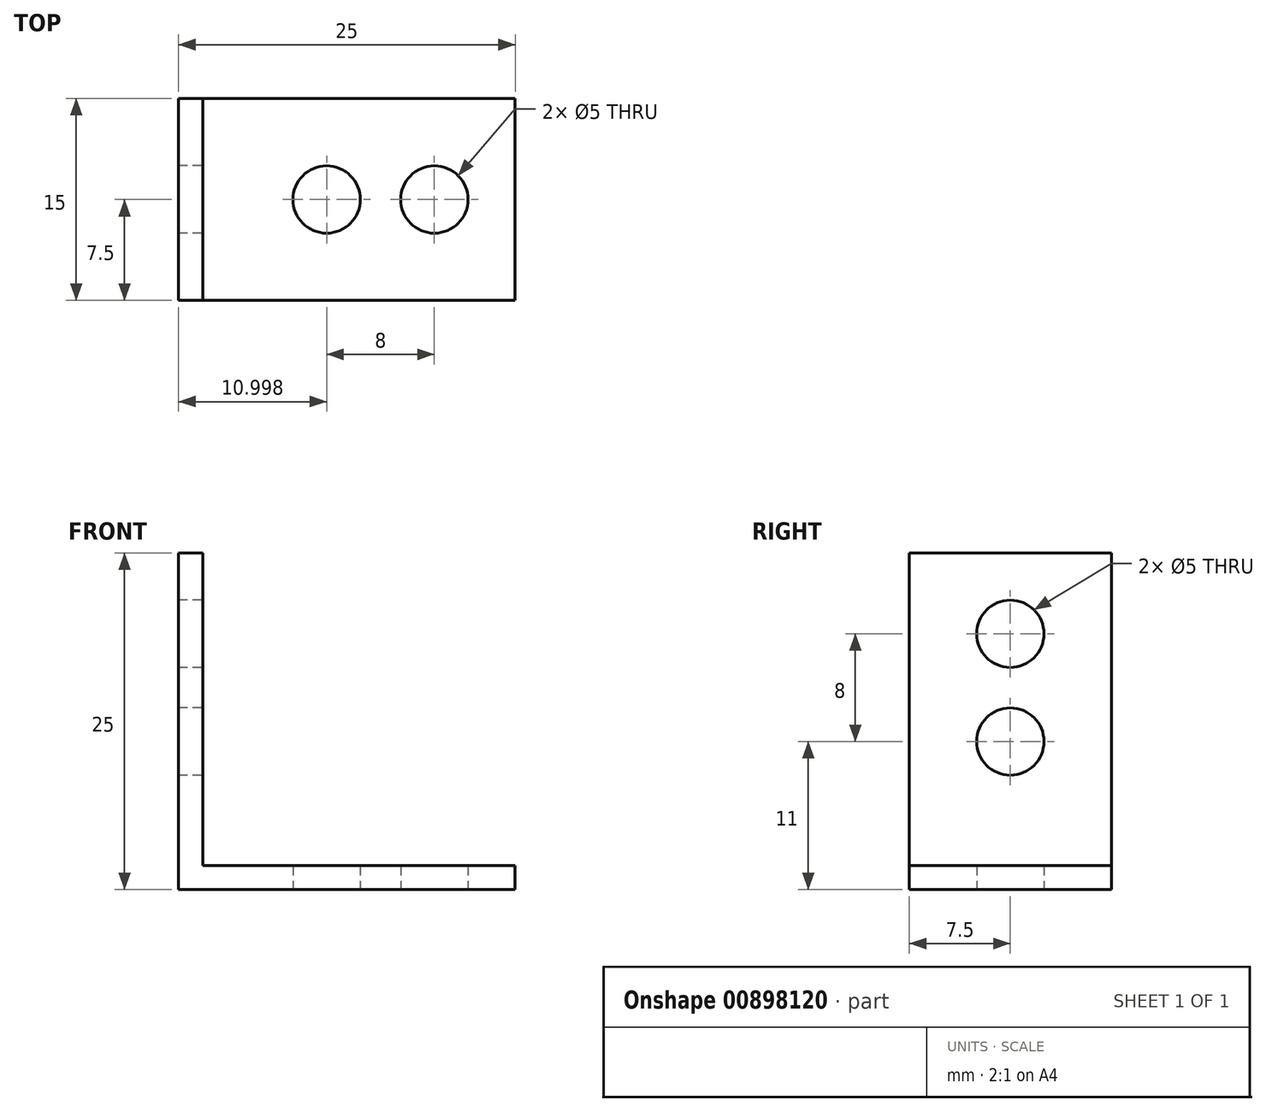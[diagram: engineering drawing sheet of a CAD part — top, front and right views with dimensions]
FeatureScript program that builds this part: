
annotation { "Feature Type Name" : "Feature", "Feature Type Description" : "" }
export const myFeature = defineFeature(function(context is Context, id is Id, definition is map)
    precondition{}
    {
        {
            var Q0;
            Q0=qCreatedBy(makeId("Front.planeOp"),FACE);
            var sketch = newSketch(context, id + "F0", { "sketchPlane" : qUnion([Q0])});
            skLineSegment(sketch, "E0.bottom", {"start": v(-6.03, 0) * mm, "end": v(18.97, 0) * mm});
            skLineSegment(sketch, "E0.top", {"start": v(-6.03, 1.8) * mm, "end": v(18.97, 1.8) * mm});
            skLineSegment(sketch, "E0.left", {"start": v(-6.03, 0) * mm, "end": v(-6.03, 1.8) * mm});
            skLineSegment(sketch, "E0.right", {"start": v(18.97, 0) * mm, "end": v(18.97, 1.8) * mm});
            skLineSegment(sketch, "E1.bottom", {"start": v(-6.03, 0) * mm, "end": v(-4.23, 0) * mm});
            skLineSegment(sketch, "E1.top", {"start": v(-6.03, 25) * mm, "end": v(-4.23, 25) * mm});
            skLineSegment(sketch, "E1.left", {"start": v(-6.03, 0) * mm, "end": v(-6.03, 25) * mm});
            skLineSegment(sketch, "E1.right", {"start": v(-4.23, 0) * mm, "end": v(-4.23, 25) * mm});
            skSolve(sketch);
        }
        {
            var Q0;
            Q0 = qSketchRegion(id + "F0", true);
            extrude(context, id + "F1", {"entities" : qUnion([Q0]), "depth" : 15 * mm, "offsetDistance" : 25 * mm});
        }
        {
            var Q0;
            Q0=makeQuery(id+"F1.opExtrude","SWEPT_FACE",FACE,{"disambiguationData":[OSD([sQuery(id+"F0.wireOp",EDGE,"E1.left")])]});
            var sketch = newSketch(context, id + "F2", { "sketchPlane" : qUnion([Q0])});
            skPoint(sketch, "E2", {"position": v(0, 25) * mm});
            skPoint(sketch, "E3", {"position": v(15, 25) * mm});
            skPoint(sketch, "E4", {"position": v(15, 0) * mm});
            skPoint(sketch, "E5", {"position": v(0, 0) * mm});
            skPoint(sketch, "E6", {"position": v(7.5, 25) * mm});
            skPoint(sketch, "E7", {"position": v(7.5, 0) * mm});
            skPoint(sketch, "E8", {"position": v(7.5, 11) * mm});
            skPoint(sketch, "E9", {"position": v(7.5, 19) * mm});
            skCircle(sketch, "E10", {"center": v(7.5, 19) * mm, "radius": 2.5 * mm});
            skCircle(sketch, "E11", {"center": v(7.5, 11) * mm, "radius": 2.5 * mm});
            skSolve(sketch);
        }
        {
            var Q0;
            Q0=makeQuery(id+"F1.opExtrude","SWEPT_FACE",FACE,{"disambiguationData":[OSD([sQuery(id+"F0.wireOp",EDGE,"E0.bottom"),sQuery(id+"F0.wireOp",EDGE,"E1.bottom")])]});
            var sketch = newSketch(context, id + "F3", { "sketchPlane" : qUnion([Q0])});
            skPoint(sketch, "E12", {"position": v(-6.03, 15) * mm});
            skPoint(sketch, "E13", {"position": v(18.97, 15) * mm});
            skPoint(sketch, "E14", {"position": v(18.97, 0) * mm});
            skPoint(sketch, "E15", {"position": v(-6.03, 0) * mm});
            skPoint(sketch, "E16", {"position": v(-6.03, 7.5) * mm});
            skPoint(sketch, "E17", {"position": v(18.97, 7.5) * mm});
            skPoint(sketch, "E18", {"position": v(4.97, 7.5) * mm});
            skPoint(sketch, "E19", {"position": v(12.97, 7.5) * mm});
            skCircle(sketch, "E20", {"center": v(12.97, 7.5) * mm, "radius": 2.5 * mm});
            skCircle(sketch, "E21", {"center": v(4.97, 7.5) * mm, "radius": 2.5 * mm});
            skSolve(sketch);
        }
        {
            var Q0;
            Q0=sQuery(id+"F2.wireOp",VERTEX,"E9");
            var Q1;
            Q1=sQuery(id+"F2.wireOp",VERTEX,"E8");
            var Q2;
            Q2=sQuery(id+"F3.wireOp",VERTEX,"E18");
            var Q3;
            Q3=sQuery(id+"F3.wireOp",VERTEX,"E19");
            var Q4;
            Q4=makeQuery(id+"F1.opExtrude","SWEPT_BODY",BODY,{"disambiguationData":[OSD([sQuery(id+"F0.wireOp",EDGE,"E0.bottom"),sQuery(id+"F0.wireOp",EDGE,"E0.top"),sQuery(id+"F0.wireOp",EDGE,"E0.right"),sQuery(id+"F0.wireOp",EDGE,"E1.bottom"),sQuery(id+"F0.wireOp",EDGE,"E1.top"),sQuery(id+"F0.wireOp",EDGE,"E1.left"),sQuery(id+"F0.wireOp",EDGE,"E1.right")])]});
            hole(context, id + "F4", {"style" : HoleStyle.SIMPLE, "endStyle" : HoleEndStyle.BLIND, "holeDiameter" : 5 * mm, "majorDiameter" : 5 * mm, "holeDepth" : 1.8 * mm, "isTappedThrough" : true, "tappedDepth" : 12 * mm, "tapClearance" : 3, "locations" : qUnion([Q0, Q1, Q2, Q3]), "scope" : qUnion([Q4])});
        }
    });
